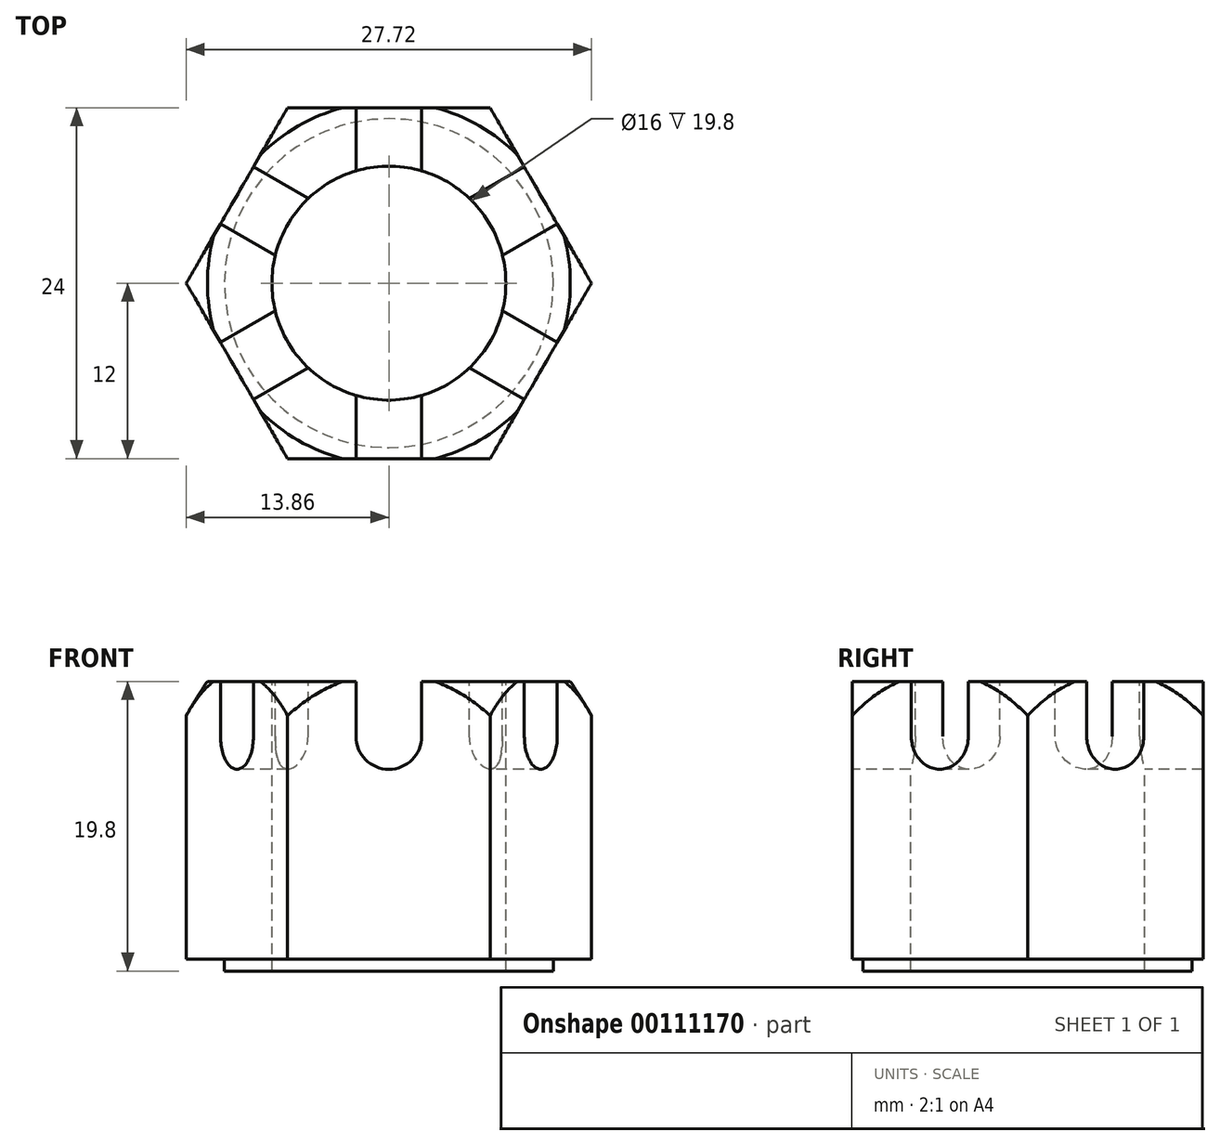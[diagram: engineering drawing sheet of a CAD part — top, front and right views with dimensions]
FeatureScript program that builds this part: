
annotation { "Feature Type Name" : "Feature", "Feature Type Description" : "" }
export const myFeature = defineFeature(function(context is Context, id is Id, definition is map)
    precondition{}
    {
        {
            var Q0;
            Q0=qCreatedBy(makeId("Top.planeOp"),FACE);
            var sketch = newSketch(context, id + "F0", { "sketchPlane" : qUnion([Q0])});
            skLineSegment(sketch, "E0", {"start": v(0, 0) * mm, "end": v(0, 12) * mm});
            skLineSegment(sketch, "E1", {"start": v(0, 0) * mm, "end": v(0, -12) * mm});
            skLineSegment(sketch, "E2", {"start": v(0, 0) * mm, "end": v(12, 0) * mm});
            skLineSegment(sketch, "E3", {"start": v(0, 0) * mm, "end": v(-12, 0) * mm});
            skPoint(sketch, "E4.endSnap0", {"position": v(0, -6) * mm});
            skPoint(sketch, "E5.endSnap0", {"position": v(0, 6) * mm});
            skCircle(sketch, "E6.cCircle", {"center": v(0, 0) * mm, "radius": 12 * mm, "construction": true});
            skLineSegment(sketch, "E6.0", {"start": v(-6.93, 12) * mm, "end": v(6.93, 12) * mm});
            skLineSegment(sketch, "E6.1", {"start": v(6.93, 12) * mm, "end": v(13.86, 0) * mm});
            skLineSegment(sketch, "E6.2", {"start": v(13.86, 0) * mm, "end": v(6.93, -12) * mm});
            skLineSegment(sketch, "E6.3", {"start": v(6.93, -12) * mm, "end": v(-6.93, -12) * mm});
            skLineSegment(sketch, "E6.4", {"start": v(-6.93, -12) * mm, "end": v(-13.86, 0) * mm});
            skLineSegment(sketch, "E6.5", {"start": v(-13.86, 0) * mm, "end": v(-6.93, 12) * mm});
            skPoint(sketch, "E6.0.midPoint", {"position": v(0, 12) * mm});
            skSolve(sketch);
        }
        {
            var Q0;
            Q0 = qSketchRegion(id + "F0", true);
            extrude(context, id + "F1", {"entities" : qUnion([Q0]), "depth" : 19 * mm});
        }
        {
            var Q0;
            Q0=makeQuery(id+"F1.opExtrude","CAP_FACE",FACE,{"disambiguationData":[OSD([sQuery(id+"F0.wireOp",EDGE,"E6.0"),sQuery(id+"F0.wireOp",EDGE,"E6.1"),sQuery(id+"F0.wireOp",EDGE,"E6.2"),sQuery(id+"F0.wireOp",EDGE,"E6.3"),sQuery(id+"F0.wireOp",EDGE,"E6.4"),sQuery(id+"F0.wireOp",EDGE,"E6.5")])],"isStart":true});
            var sketch = newSketch(context, id + "F2", { "sketchPlane" : qUnion([Q0])});
            skCircle(sketch, "E7", {"center": v(0, 0) * mm, "radius": 11.25 * mm});
            skSolve(sketch);
        }
        {
            var Q0;
            Q0 = qSketchRegion(id + "F2", true);
            extrude(context, id + "F3", {"entities" : qUnion([Q0]), "operationType" : NewBodyOperationType.ADD, "depth" : 0.8 * mm});
        }
        {
            var Q0;
            Q0=makeQuery(id+"F1.opExtrude","CAP_FACE",FACE,{"disambiguationData":[OSD([sQuery(id+"F0.wireOp",EDGE,"E6.0"),sQuery(id+"F0.wireOp",EDGE,"E6.1"),sQuery(id+"F0.wireOp",EDGE,"E6.2"),sQuery(id+"F0.wireOp",EDGE,"E6.3"),sQuery(id+"F0.wireOp",EDGE,"E6.4"),sQuery(id+"F0.wireOp",EDGE,"E6.5")])],"isStart":false});
            var sketch = newSketch(context, id + "F4", { "sketchPlane" : qUnion([Q0])});
            skCircle(sketch, "E8", {"center": v(0, 0) * mm, "radius": 8 * mm});
            skSolve(sketch);
        }
        {
            var Q0;
            Q0 = qSketchRegion(id + "F4", true);
            extrude(context, id + "F5", {"entities" : qUnion([Q0]), "operationType" : NewBodyOperationType.REMOVE, "oppositeDirection" : true, "depth" : (19 - 2) * mm});
        }
        {
            var Q0;
            Q0=makeQuery(id+"F1.opExtrude","SWEPT_FACE",FACE,{"disambiguationData":[OSD([sQuery(id+"F0.wireOp",EDGE,"E6.3")])]});
            var sketch = newSketch(context, id + "F6", { "sketchPlane" : qUnion([Q0])});
            skLineSegment(sketch, "E9", {"start": v(-2.25, 19) * mm, "end": v(2.25, 19) * mm});
            skLineSegment(sketch, "E10", {"start": v(0, 19) * mm, "end": v(0, 15.25) * mm});
            skPoint(sketch, "E10.endSnap0", {"position": v(0, 19) * mm});
            skArc(sketch, "E11", {"start": v(-2.25, 15.25) * mm, "mid": v(0, 13) * mm, "end": v(2.25, 15.25) * mm});
            skLineSegment(sketch, "E12", {"start": v(-2.25, 15.25) * mm, "end": v(-2.25, 19) * mm});
            skLineSegment(sketch, "E13", {"start": v(2.25, 15.25) * mm, "end": v(2.25, 19) * mm});
            skSolve(sketch);
        }
        {
            var Q0;
            Q0 = qSketchRegion(id + "F6", true);
            extrude(context, id + "F7", {"entities" : qUnion([Q0]), "operationType" : NewBodyOperationType.REMOVE, "oppositeDirection" : true, "depth" : 25 * mm});
        }
        {
            var Q0;
            Q0=makeQuery(id+"F1.opExtrude","SWEPT_FACE",FACE,{"disambiguationData":[OSD([sQuery(id+"F0.wireOp",EDGE,"E6.4")])]});
            var sketch = newSketch(context, id + "F8", { "sketchPlane" : qUnion([Q0])});
            skLineSegment(sketch, "E14", {"start": v(0, 19) * mm, "end": v(2.25, 19) * mm});
            skLineSegment(sketch, "E15", {"start": v(0, 19) * mm, "end": v(-2.25, 19) * mm});
            skLineSegment(sketch, "E16", {"start": v(-2.25, 19) * mm, "end": v(-2.25, 15.25) * mm});
            skLineSegment(sketch, "E17", {"start": v(2.25, 15.25) * mm, "end": v(2.25, 19) * mm});
            skArc(sketch, "E18", {"start": v(2.25, 15.25) * mm, "mid": v(0, 13) * mm, "end": v(-2.25, 15.25) * mm});
            skSolve(sketch);
        }
        {
            var Q0;
            Q0 = qSketchRegion(id + "F8", true);
            extrude(context, id + "F9", {"entities" : qUnion([Q0]), "operationType" : NewBodyOperationType.REMOVE, "oppositeDirection" : true, "depth" : 25 * mm});
        }
        {
            var Q0;
            Q0=makeQuery(id+"F1.opExtrude","SWEPT_FACE",FACE,{"disambiguationData":[OSD([sQuery(id+"F0.wireOp",EDGE,"E6.2")])]});
            var sketch = newSketch(context, id + "F10", { "sketchPlane" : qUnion([Q0])});
            skLineSegment(sketch, "E19", {"start": v(0, 19) * mm, "end": v(0, 15.25) * mm});
            skPoint(sketch, "E19.endSnap0", {"position": v(0, 19) * mm});
            skArc(sketch, "E20", {"start": v(2.25, 15.25) * mm, "mid": v(0, 13) * mm, "end": v(-2.25, 15.25) * mm});
            skLineSegment(sketch, "E21", {"start": v(-2.25, 15.25) * mm, "end": v(-2.25, 19) * mm});
            skLineSegment(sketch, "E22", {"start": v(-2.25, 19) * mm, "end": v(2.25, 19) * mm});
            skLineSegment(sketch, "E23", {"start": v(2.25, 19) * mm, "end": v(2.25, 15.25) * mm});
            skSolve(sketch);
        }
        {
            var Q0;
            Q0 = qSketchRegion(id + "F10", true);
            extrude(context, id + "F11", {"entities" : qUnion([Q0]), "operationType" : NewBodyOperationType.REMOVE, "oppositeDirection" : true, "depth" : 30.06 * mm});
        }
        {
            var Q0;
            Q0=qCreatedBy(makeId("Front.planeOp"),FACE);
            var sketch = newSketch(context, id + "F12", { "sketchPlane" : qUnion([Q0])});
            skArc(sketch, "E24", {"start": v(16.17, 10.28) * mm, "mid": v(13.28, 17.66) * mm, "end": v(8.08, 23.64) * mm});
            skLineSegment(sketch, "E25", {"start": v(8.08, 23.64) * mm, "end": v(18.86, 27.86) * mm});
            skLineSegment(sketch, "E26", {"start": v(18.86, 27.86) * mm, "end": v(16.17, 10.28) * mm});
            skLineSegment(sketch, "E27", {"start": v(0, 0) * mm, "end": v(0, -40.48) * mm});
            skSolve(sketch);
        }
        {
            var Q0;
            Q0=makeQuery(id+"F12.imprint","IMPRINT",FACE,{"disambiguationData":[TD([[makeQuery(id+"F12.imprint","IMPRINT",EDGE,{"derivedFrom":sQuery(id+"F12.wireOp",EDGE,"E24")}),-1.0]])]});
            var Q1;
            Q1=sQuery(id+"F12.wireOp",EDGE,"E27");
            revolve(context, id + "F13", {"operationType" : NewBodyOperationType.REMOVE, "entities" : qUnion([Q0]), "axis" : qUnion([Q1]), "revolveType" : RevolveType.FULL, "oppositeDirection" : true});
        }
        {
            var Q0;
            Q0=makeQuery(id+"F3.opExtrude","CAP_FACE",FACE,{"disambiguationData":[OSD([sQuery(id+"F2.wireOp",EDGE,"E7")])],"isStart":false});
            var sketch = newSketch(context, id + "F14", { "sketchPlane" : qUnion([Q0])});
            skCircle(sketch, "E28", {"center": v(0, 0) * mm, "radius": 8 * mm});
            skSolve(sketch);
        }
        {
            var Q0;
            Q0 = qSketchRegion(id + "F14", true);
            extrude(context, id + "F15", {"entities" : qUnion([Q0]), "operationType" : NewBodyOperationType.REMOVE, "oppositeDirection" : true, "depth" : 25 * mm});
        }
    });
